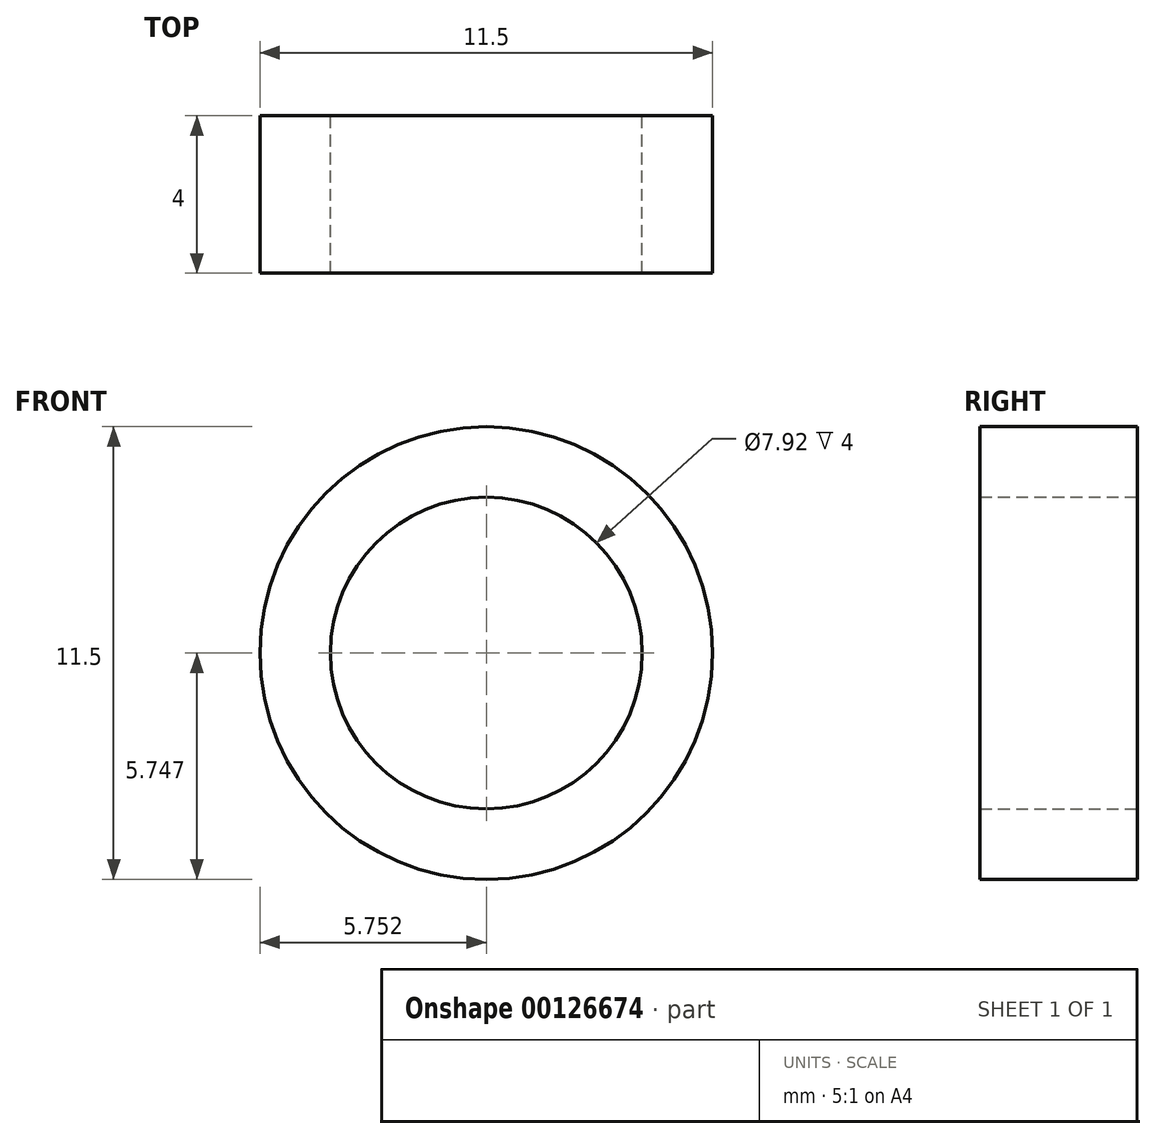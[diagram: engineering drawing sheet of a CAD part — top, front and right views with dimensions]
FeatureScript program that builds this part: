
annotation { "Feature Type Name" : "Feature", "Feature Type Description" : "" }
export const myFeature = defineFeature(function(context is Context, id is Id, definition is map)
    precondition{}
    {
        {
            var Q0;
            Q0=qCreatedBy(makeId("Front.planeOp"),FACE);
            var sketch = newSketch(context, id + "F0", { "sketchPlane" : qUnion([Q0])});
            skCircle(sketch, "E0", {"center": v(-34.14, 34.13) * mm, "radius": 3.96 * mm});
            skCircle(sketch, "E1", {"center": v(-34.14, 34.13) * mm, "radius": 5.75 * mm});
            skSolve(sketch);
        }
        {
            var Q0;
            Q0=makeQuery(id+"F0.imprint","IMPRINT",FACE,{"disambiguationData":[TD([[makeQuery(id+"F0.imprint","IMPRINT",EDGE,{"derivedFrom":sQuery(id+"F0.wireOp",EDGE,"E0")}),-1.0]])]});
            extrude(context, id + "F1", {"entities" : qUnion([Q0]), "depth" : 4 * mm});
        }
    });
